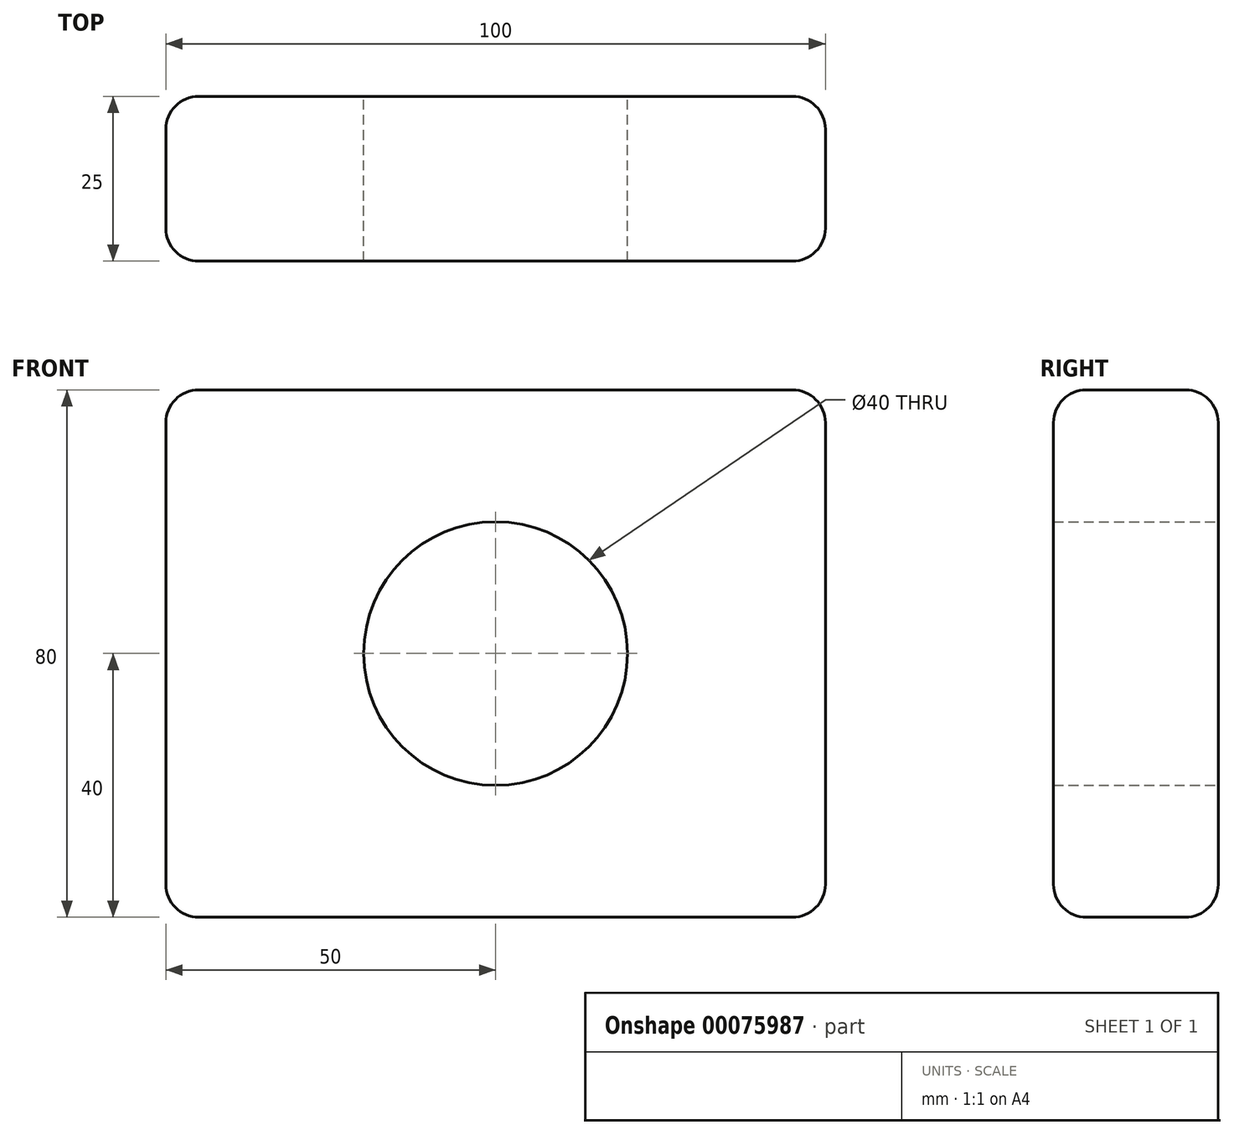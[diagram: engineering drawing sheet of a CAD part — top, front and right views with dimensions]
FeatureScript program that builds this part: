
annotation { "Feature Type Name" : "Feature", "Feature Type Description" : "" }
export const myFeature = defineFeature(function(context is Context, id is Id, definition is map)
    precondition{}
    {
        {
            var Q0;
            Q0=qCreatedBy(makeId("Front.planeOp"),FACE);
            var sketch = newSketch(context, id + "F0", { "sketchPlane" : qUnion([Q0])});
            skLineSegment(sketch, "E0.bottom", {"start": v(50, 40) * mm, "end": v(-50, 40) * mm});
            skLineSegment(sketch, "E0.top", {"start": v(50, -40) * mm, "end": v(-50, -40) * mm});
            skLineSegment(sketch, "E0.left", {"start": v(50, 40) * mm, "end": v(50, -40) * mm});
            skLineSegment(sketch, "E0.right", {"start": v(-50, 40) * mm, "end": v(-50, -40) * mm});
            skPoint(sketch, "E0.middle", {"position": v(0, 0) * mm});
            skCircle(sketch, "E1", {"center": v(0, 0) * mm, "radius": 20 * mm});
            skSolve(sketch);
        }
        {
            var Q0;
            Q0=makeQuery(id+"F0.imprint","IMPRINT",FACE,{"disambiguationData":[TD([[makeQuery(id+"F0.imprint","IMPRINT",EDGE,{"derivedFrom":sQuery(id+"F0.wireOp",EDGE,"E0.bottom")}),1.0]])]});
            extrude(context, id + "F1", {"entities" : qUnion([Q0]), "depth" : 25 * mm});
        }
        {
            var Q0;
            Q0=makeQuery(id+"F1.opExtrude","SWEPT_FACE",FACE,{"disambiguationData":[OSD([sQuery(id+"F0.wireOp",EDGE,"E0.left")])]});
            var Q1;
            Q1=makeQuery(id+"F1.opExtrude","SWEPT_FACE",FACE,{"disambiguationData":[OSD([sQuery(id+"F0.wireOp",EDGE,"E0.bottom")])]});
            var Q2;
            Q2=makeQuery(id+"F1.opExtrude","SWEPT_FACE",FACE,{"disambiguationData":[OSD([sQuery(id+"F0.wireOp",EDGE,"E0.right")])]});
            var Q3;
            Q3=makeQuery(id+"F1.opExtrude","SWEPT_FACE",FACE,{"disambiguationData":[OSD([sQuery(id+"F0.wireOp",EDGE,"E0.top")])]});
            fillet(context, id + "F2", {"entities" : qUnion([Q0, Q1, Q2, Q3]), "radius" : 5 * mm, "tangentPropagation" : true, "allowEdgeOverflow" : false});
        }
    });
